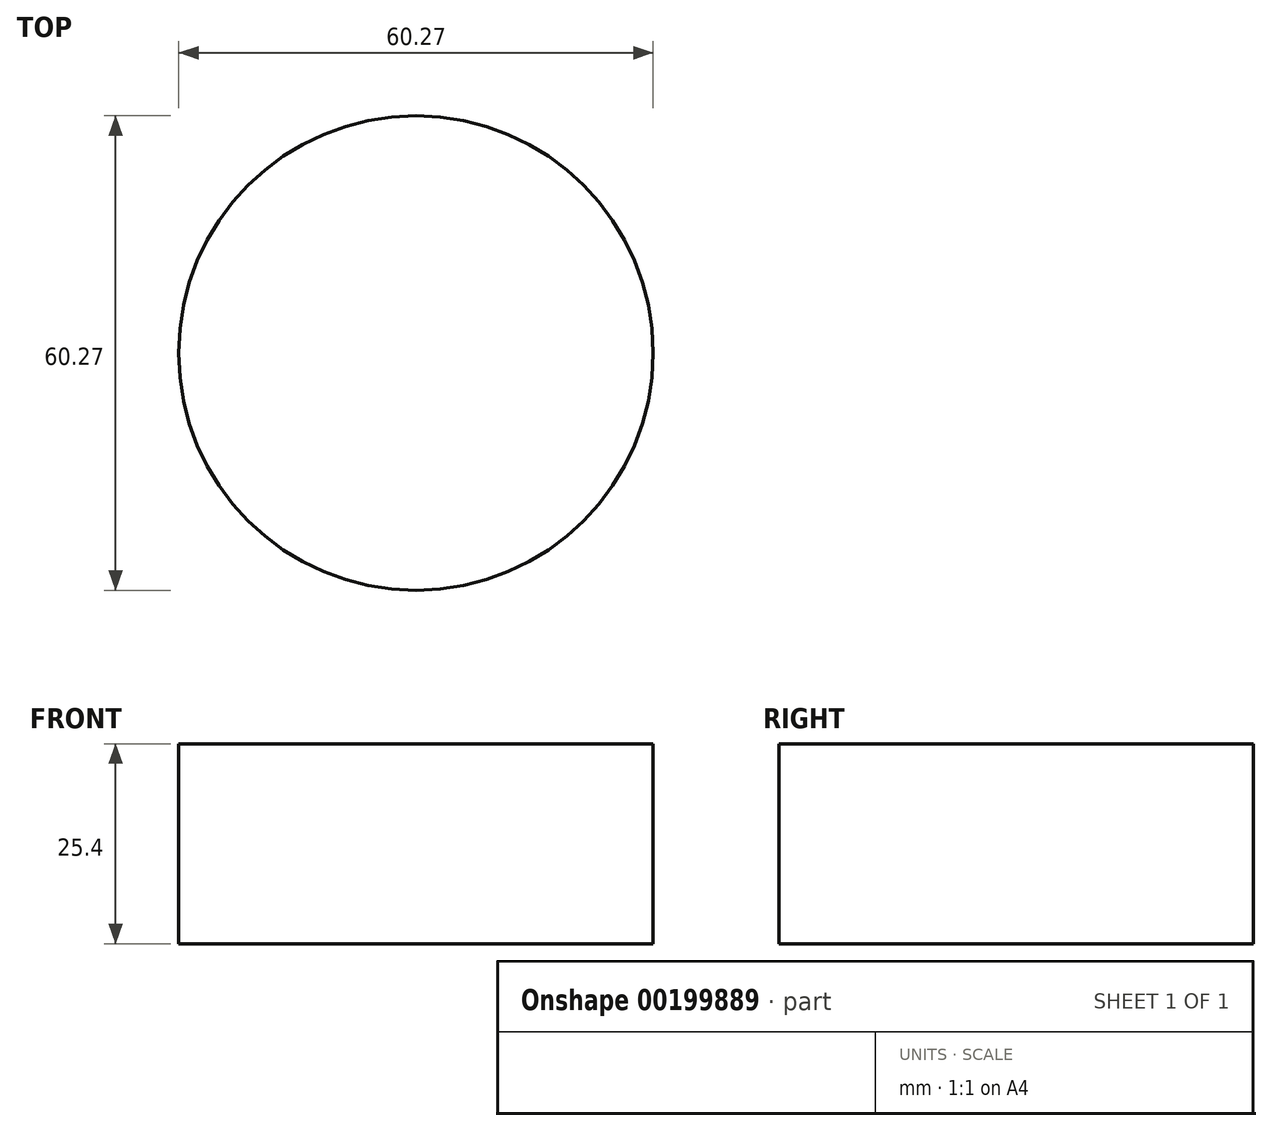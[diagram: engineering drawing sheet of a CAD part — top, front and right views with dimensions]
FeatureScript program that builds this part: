
annotation { "Feature Type Name" : "Feature", "Feature Type Description" : "" }
export const myFeature = defineFeature(function(context is Context, id is Id, definition is map)
    precondition{}
    {
        {
            var Q0;
            Q0=qCreatedBy(makeId("Top.planeOp"),FACE);
            var sketch = newSketch(context, id + "F0", { "sketchPlane" : qUnion([Q0])});
            skCircle(sketch, "E0", {"center": v(-46.98, 26.8) * mm, "radius": 30.14 * mm});
            skSolve(sketch);
        }
        {
            var Q0;
            Q0=makeQuery(id+"F0.imprint","IMPRINT",FACE,{"disambiguationData":[TD([[makeQuery(id+"F0.imprint","IMPRINT",EDGE,{"derivedFrom":sQuery(id+"F0.wireOp",EDGE,"E0")}),1.0]])]});
            var Q1;
            Q1=sQuery(id+"F0.wireOp",EDGE,"E0");
            extrude(context, id + "F1", {"entities" : qUnion([Q0]), "surfaceEntities" : qUnion([Q1]), "depth" : 25.4 * mm});
        }
        {
            var Q0;
            Q0=qCreatedBy(makeId("Top.planeOp"),FACE);
            var sketch = newSketch(context, id + "F2", { "sketchPlane" : qUnion([Q0])});
            skCircle(sketch, "E1", {"center": v(42.99, 32.75) * mm, "radius": 76.7 * mm});
            skCircle(sketch, "E2", {"center": v(-56.37, -22.51) * mm, "radius": 50.73 * mm});
            skSolve(sketch);
        }
        {
            var Q0;
            Q0=sQuery(id+"F2.wireOp",EDGE,"E1");
            extrude(context, id + "F3", {"bodyType" : ToolBodyType.SURFACE, "surfaceEntities" : qUnion([Q0]), "depth" : 25.4 * mm});
        }
    });
